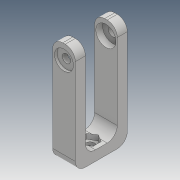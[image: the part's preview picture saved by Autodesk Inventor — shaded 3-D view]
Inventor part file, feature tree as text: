
AUTODESK INVENTOR PART (.ipt)
format: ipt  version: 2017 (Build 210142000, 142)  size: 205,824 bytes
history: native  units: mm
features: extrude x10, sketch x10, fillet x3, other x1, projected_geometry x1
ambient origin geometry x8: Origin, YZ Plane, XZ Plane, XY Plane, X Axis, Y Axis, Z Axis, Center Point
bodies: Body1 (feature_tree)
feature tree (25):
  other  "Sólido1"
  extrude  "Extrusión1"  Depth=6.0mm TaperAngle=0.0deg
  extrude  "Extrusión2"  Depth=115.0mm TaperAngle=0.0deg
  extrude  "Extrusión3"  Depth=17.0mm
  extrude  "Extrusión4"  Depth=27.0mm
  extrude  "Extrusión8"  Depth=12.0mm
  extrude  "Extrusión9"  Depth=10.0mm TaperAngle=0.0deg
  extrude  "Extrusión10"  Depth=2.5mm TaperAngle=0.0deg
  extrude  "Extrusión11"  Depth=3.0mm TaperAngle=0.0deg
  extrude  "Extrusión12"  Depth=10.0mm
  extrude  "Extrusión13"  Depth=12.0mm
  fillet  "Empalme4"  Radius=8.0mm
  fillet  "Empalme5"  Radius=16.0mm
  fillet  "Empalme6"  Radius=12.0mm
  sketch  "Boceto1"  dims[d0=6.0mm d1=0.0mm d2=6.0mm d3=0.0mm]
  sketch  "Boceto2"  dims[d5=3.0mm d6=0.0mm d7=115.0mm d8=0.0mm]
  projected_geometry  "Contorno proyectado1"
  sketch  "Boceto3"  dims[d18=11.0mm d20=17.0mm]
  sketch  "Boceto5"  dims[d21=5.0mm d22=27.0mm]
  sketch  "Boceto9"  dims[d23=62.0mm d24=12.0mm]
  sketch  "Boceto10"  dims[d25=10.0mm d26=10.0mm d27=0.0mm]
  sketch  "Boceto11"  dims[d29=22.0mm d30=2.5mm d31=0.0mm]
  sketch  "Boceto12"  dims[d32=12.0mm d34=3.0mm d35=0.0mm]
  sketch  "Boceto14"  dims[d36=3.0mm d37=0.0mm d38=10.0mm]
  sketch  "Boceto15"  dims[d39=3.0mm d40=0.0mm d41=24.0mm d42=8.0mm d43=0.0mm d45=16.0mm d46=12.0mm d47=12.0mm d48=12.0mm]
